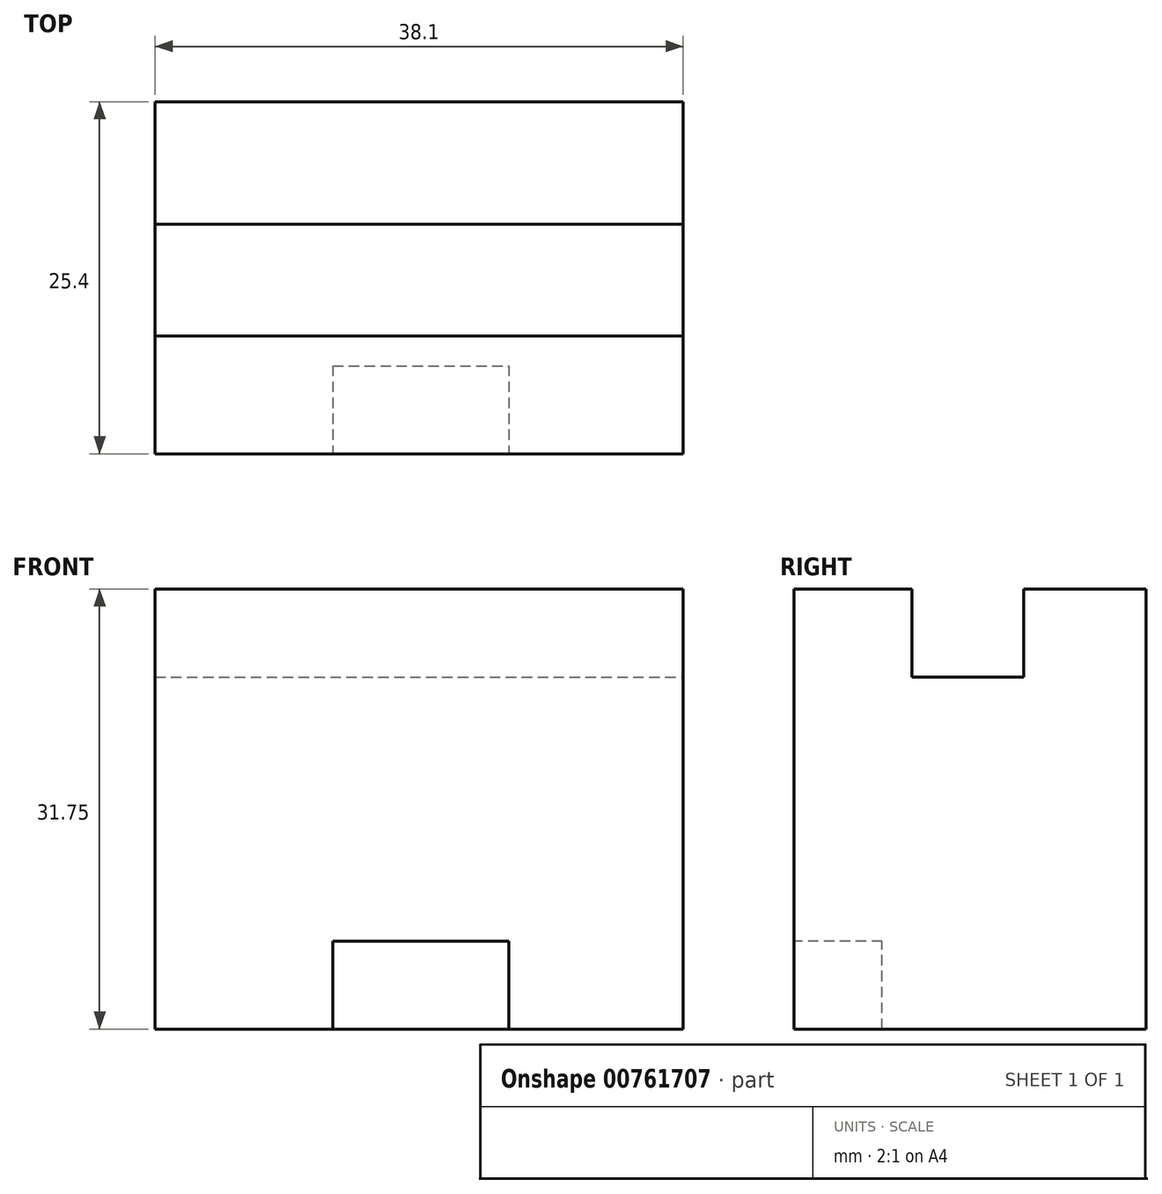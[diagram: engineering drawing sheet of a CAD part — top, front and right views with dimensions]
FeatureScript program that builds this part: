
annotation { "Feature Type Name" : "Feature", "Feature Type Description" : "" }
export const myFeature = defineFeature(function(context is Context, id is Id, definition is map)
    precondition{}
    {
        {
            var Q0;
            Q0=qCreatedBy(makeId("Front.planeOp"),FACE);
            var sketch = newSketch(context, id + "F0", { "sketchPlane" : qUnion([Q0])});
            skLineSegment(sketch, "E0", {"start": v(0, 0) * mm, "end": v(0, 31.75) * mm});
            skLineSegment(sketch, "E1", {"start": v(0, 31.75) * mm, "end": v(38.1, 31.75) * mm});
            skLineSegment(sketch, "E2", {"start": v(38.1, 31.75) * mm, "end": v(38.1, 0) * mm});
            skLineSegment(sketch, "E3", {"start": v(0, 0) * mm, "end": v(38.1, 0) * mm});
            skSolve(sketch);
        }
        {
            var Q0;
            Q0=makeQuery(id+"F0.imprint","IMPRINT",FACE,{"disambiguationData":[TD([[makeQuery(id+"F0.imprint","IMPRINT",EDGE,{"derivedFrom":sQuery(id+"F0.wireOp",EDGE,"E0")}),-1.0]])]});
            extrude(context, id + "F1", {"entities" : qUnion([Q0]), "depth" : 25.4 * mm, "offsetDistance" : 25.4 * mm});
        }
        {
            var Q0;
            Q0=makeQuery(id+"F1.opExtrude","SWEPT_FACE",FACE,{"disambiguationData":[OSD([sQuery(id+"F0.wireOp",EDGE,"E1")])]});
            var sketch = newSketch(context, id + "F2", { "sketchPlane" : qUnion([Q0])});
            skLineSegment(sketch, "E4", {"start": v(0, -8.84) * mm, "end": v(38.1, -8.84) * mm});
            skLineSegment(sketch, "E5", {"start": v(0, -16.9) * mm, "end": v(38.1, -16.9) * mm});
            skSolve(sketch);
        }
        {
            var Q0;
            {var subQ0=sQuery(id+"F2.wireOp",EDGE,"E4");Q0=makeQuery(id+"F2.imprint","IMPRINT",FACE,{"disambiguationData":[TD([[makeQuery(id+"F2.imprint","IMPRINT",EDGE,{"derivedFrom":subQ0}),-1.0]])]});}
            extrude(context, id + "F3", {"entities" : qUnion([Q0]), "operationType" : NewBodyOperationType.REMOVE, "oppositeDirection" : true, "depth" : 6.35 * mm, "offsetDistance" : 25.4 * mm});
        }
        {
            var Q0;
            Q0=makeQuery(id+"F1.opExtrude","CAP_FACE",FACE,{"disambiguationData":[OSD([sQuery(id+"F0.wireOp",EDGE,"E0"),sQuery(id+"F0.wireOp",EDGE,"E1"),sQuery(id+"F0.wireOp",EDGE,"E2"),sQuery(id+"F0.wireOp",EDGE,"E3")])],"isStart":false});
            var sketch = newSketch(context, id + "F4", { "sketchPlane" : qUnion([Q0])});
            skLineSegment(sketch, "E6", {"start": v(12.82, 0) * mm, "end": v(12.82, 6.35) * mm});
            skLineSegment(sketch, "E7", {"start": v(12.82, 6.35) * mm, "end": v(25.52, 6.35) * mm});
            skLineSegment(sketch, "E8", {"start": v(25.52, 6.35) * mm, "end": v(25.52, 0) * mm});
            skLineSegment(sketch, "E9", {"start": v(12.82, 0) * mm, "end": v(25.52, 0) * mm});
            skSolve(sketch);
        }
        {
            var Q0;
            Q0=makeQuery(id+"F4.imprint","IMPRINT",FACE,{"disambiguationData":[TD([[makeQuery(id+"F4.imprint","IMPRINT",EDGE,{"derivedFrom":sQuery(id+"F4.wireOp",EDGE,"E6")}),-1.0]])]});
            extrude(context, id + "F5", {"entities" : qUnion([Q0]), "operationType" : NewBodyOperationType.REMOVE, "oppositeDirection" : true, "depth" : 6.35 * mm, "offsetDistance" : 25.4 * mm});
        }
    });
